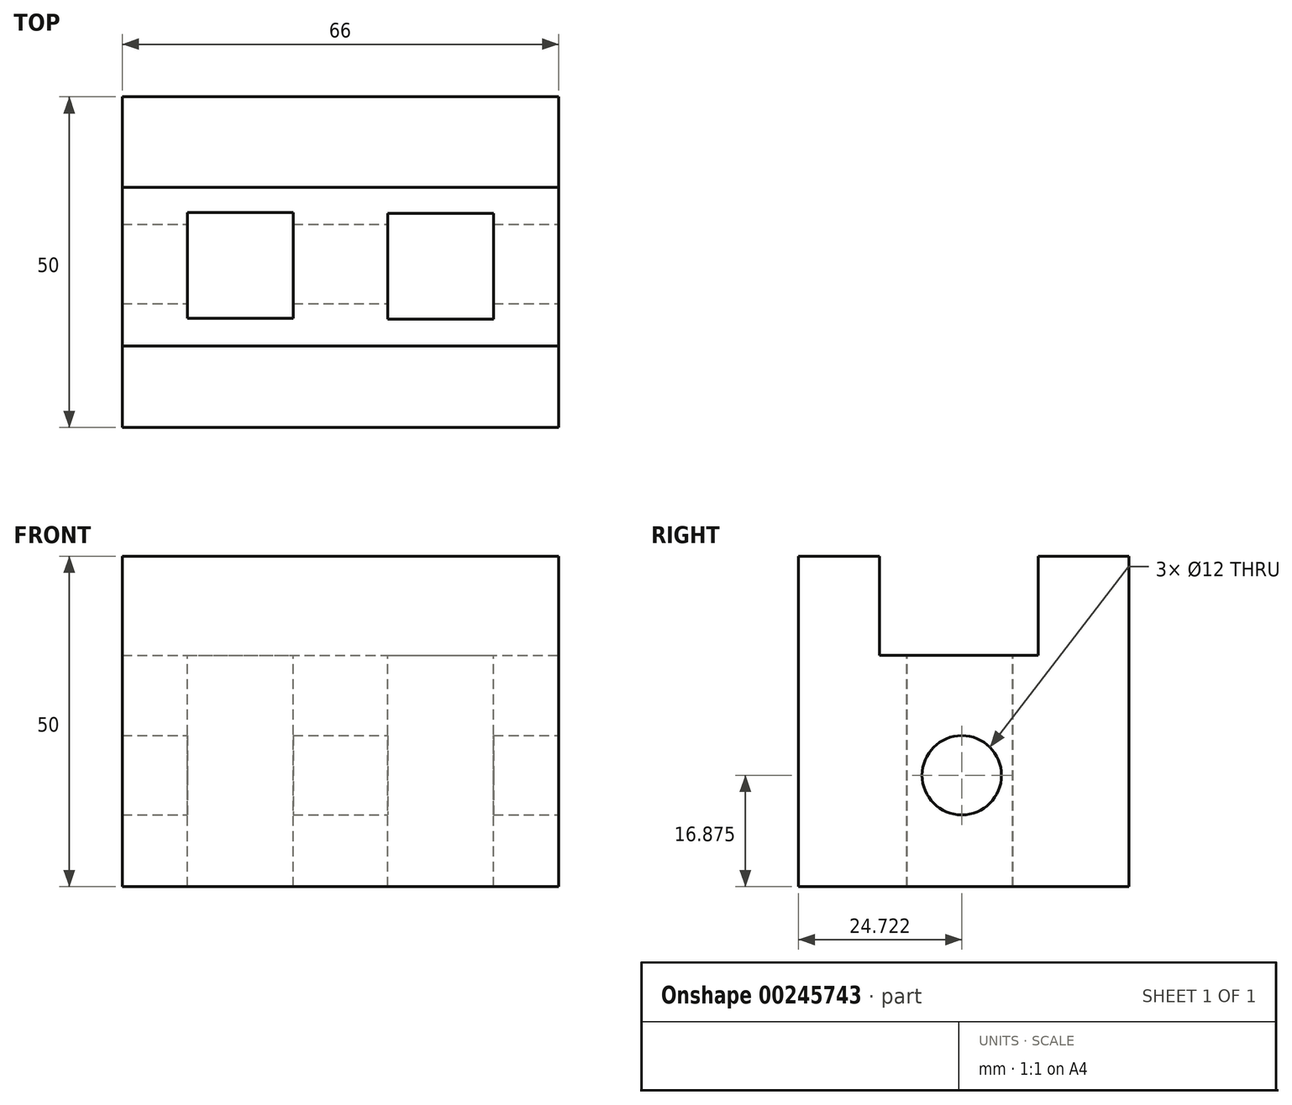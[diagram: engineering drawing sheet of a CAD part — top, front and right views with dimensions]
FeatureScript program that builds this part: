
annotation { "Feature Type Name" : "Feature", "Feature Type Description" : "" }
export const myFeature = defineFeature(function(context is Context, id is Id, definition is map)
    precondition{}
    {
        {
            var Q0;
            Q0=qCreatedBy(makeId("Top.planeOp"),FACE);
            var sketch = newSketch(context, id + "F0", { "sketchPlane" : qUnion([Q0])});
            skLineSegment(sketch, "E0.bottom", {"start": v(-51.66, -12.14) * mm, "end": v(14.34, -12.14) * mm});
            skLineSegment(sketch, "E0.top", {"start": v(-51.66, 37.86) * mm, "end": v(14.34, 37.86) * mm});
            skLineSegment(sketch, "E0.left", {"start": v(-51.66, -12.14) * mm, "end": v(-51.66, 37.86) * mm});
            skLineSegment(sketch, "E0.right", {"start": v(14.34, -12.14) * mm, "end": v(14.34, 37.86) * mm});
            skSolve(sketch);
        }
        {
            var Q0;
            Q0=makeQuery(id+"F0.imprint","IMPRINT",FACE,{"disambiguationData":[TD([[makeQuery(id+"F0.imprint","IMPRINT",EDGE,{"derivedFrom":sQuery(id+"F0.wireOp",EDGE,"E0.bottom")}),1.0]])]});
            extrude(context, id + "F1", {"entities" : qUnion([Q0]), "depth" : 50 * mm});
        }
        {
            var Q0;
            Q0=makeQuery(id+"F1.opExtrude","SWEPT_FACE",FACE,{"disambiguationData":[OSD([sQuery(id+"F0.wireOp",EDGE,"E0.right")])]});
            var sketch = newSketch(context, id + "F2", { "sketchPlane" : qUnion([Q0])});
            skLineSegment(sketch, "E1.bottom", {"start": v(0.15, 35) * mm, "end": v(24.15, 35) * mm});
            skLineSegment(sketch, "E1.top", {"start": v(0.15, 50) * mm, "end": v(24.15, 50) * mm});
            skLineSegment(sketch, "E1.left", {"start": v(0.15, 35) * mm, "end": v(0.15, 50) * mm});
            skLineSegment(sketch, "E1.right", {"start": v(24.15, 35) * mm, "end": v(24.15, 50) * mm});
            skSolve(sketch);
        }
        {
            var Q0;
            Q0=makeQuery(id+"F2.imprint","IMPRINT",FACE,{"disambiguationData":[TD([[makeQuery(id+"F2.imprint","IMPRINT",EDGE,{"derivedFrom":sQuery(id+"F2.wireOp",EDGE,"E1.bottom")}),1.0]])]});
            extrude(context, id + "F3", {"entities" : qUnion([Q0]), "operationType" : NewBodyOperationType.REMOVE, "oppositeDirection" : true, "depth" : 66 * mm});
        }
        {
            var Q0;
            Q0=makeQuery(id+"F1.opExtrude","SWEPT_FACE",FACE,{"disambiguationData":[OSD([sQuery(id+"F0.wireOp",EDGE,"E0.right")])]});
            var sketch = newSketch(context, id + "F4", { "sketchPlane" : qUnion([Q0])});
            skLineSegment(sketch, "E2", {"start": v(-12.14, 0) * mm, "end": v(12.86, 0) * mm});
            skLineSegment(sketch, "E3", {"start": v(12.86, 0) * mm, "end": v(12.86, 17) * mm});
            skSolve(sketch);
        }
        {
            var Q0;
            {var subQ4=sQuery(id+"F4.wireOp",EDGE,"E2");Q0=makeQuery(id+"F4.imprint","IMPRINT",FACE,{"disambiguationData":[TD([[makeQuery(id+"F4.imprint","IMPRINT",EDGE,{"derivedFrom":subQ4}),1.0]])]});}
            var sketch = newSketch(context, id + "F5", { "sketchPlane" : qUnion([Q0])});
            skCircle(sketch, "E4", {"center": v(12.58, 16.88) * mm, "radius": 6 * mm});
            skSolve(sketch);
        }
        {
            var Q0;
            Q0=makeQuery(id+"F5.imprint","IMPRINT",FACE,{"disambiguationData":[TD([[makeQuery(id+"F5.imprint","IMPRINT",EDGE,{"derivedFrom":sQuery(id+"F5.wireOp",EDGE,"E4")}),1.0]])]});
            extrude(context, id + "F6", {"entities" : qUnion([Q0]), "operationType" : NewBodyOperationType.REMOVE, "oppositeDirection" : true, "depth" : 66 * mm});
        }
        {
            var Q0;
            Q0=makeQuery(id+"F3.boolean.opBoolean","COPY",FACE,{"derivedFrom":makeQuery(id+"F3.opExtrude","SWEPT_FACE",FACE,{"disambiguationData":[OSD([sQuery(id+"F2.wireOp",EDGE,"E1.bottom")])]})});
            var sketch = newSketch(context, id + "F7", { "sketchPlane" : qUnion([Q0])});
            skLineSegment(sketch, "E5.bottom", {"start": v(-41.8, 20.35) * mm, "end": v(-25.8, 20.35) * mm});
            skLineSegment(sketch, "E5.top", {"start": v(-41.8, 4.35) * mm, "end": v(-25.8, 4.35) * mm});
            skLineSegment(sketch, "E5.left", {"start": v(-41.8, 20.35) * mm, "end": v(-41.8, 4.35) * mm});
            skLineSegment(sketch, "E5.right", {"start": v(-25.8, 20.35) * mm, "end": v(-25.8, 4.35) * mm});
            skLineSegment(sketch, "E6.bottom", {"start": v(-11.5, 20.25) * mm, "end": v(4.5, 20.25) * mm});
            skLineSegment(sketch, "E6.top", {"start": v(-11.5, 4.25) * mm, "end": v(4.5, 4.25) * mm});
            skLineSegment(sketch, "E6.left", {"start": v(-11.5, 20.25) * mm, "end": v(-11.5, 4.25) * mm});
            skLineSegment(sketch, "E6.right", {"start": v(4.5, 20.25) * mm, "end": v(4.5, 4.25) * mm});
            skSolve(sketch);
        }
        {
            var Q0;
            Q0=makeQuery(id+"F7.imprint","IMPRINT",FACE,{"disambiguationData":[TD([[makeQuery(id+"F7.imprint","IMPRINT",EDGE,{"derivedFrom":sQuery(id+"F7.wireOp",EDGE,"E5.bottom")}),-1.0]])]});
            var Q1;
            Q1=makeQuery(id+"F7.imprint","IMPRINT",FACE,{"disambiguationData":[TD([[makeQuery(id+"F7.imprint","IMPRINT",EDGE,{"derivedFrom":sQuery(id+"F7.wireOp",EDGE,"E6.bottom")}),-1.0]])]});
            extrude(context, id + "F8", {"entities" : qUnion([Q0, Q1]), "operationType" : NewBodyOperationType.REMOVE, "oppositeDirection" : true, "depth" : 50 * mm});
        }
    });
